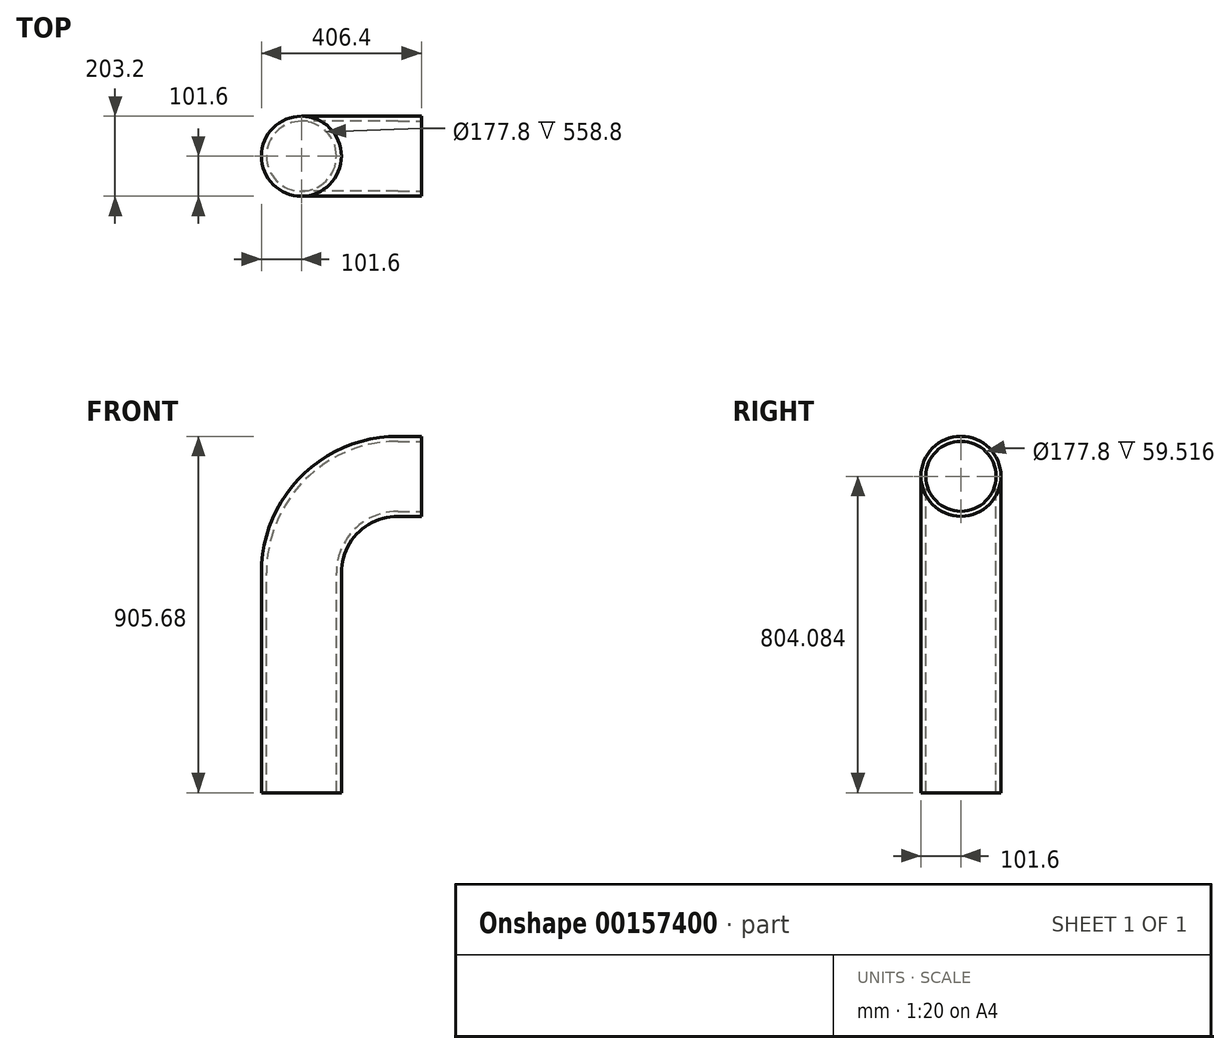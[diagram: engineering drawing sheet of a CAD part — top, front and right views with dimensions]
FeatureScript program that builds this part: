
annotation { "Feature Type Name" : "Feature", "Feature Type Description" : "" }
export const myFeature = defineFeature(function(context is Context, id is Id, definition is map)
    precondition{}
    {
        {
            var Q0;
            Q0=qCreatedBy(makeId("Front.planeOp"),FACE);
            var sketch = newSketch(context, id + "F0", { "sketchPlane" : qUnion([Q0])});
            skLineSegment(sketch, "E0.bottom", {"start": v(0, 0) * mm, "end": v(203.2, 0) * mm});
            skLineSegment(sketch, "E0.left", {"start": v(0, 0) * mm, "end": v(0, 558.8) * mm});
            skLineSegment(sketch, "E0.right", {"start": v(203.2, 0) * mm, "end": v(203.2, 558.8) * mm});
            skLineSegment(sketch, "E1.bottom", {"start": v(346.88, 905.68) * mm, "end": v(609.6, 905.68) * mm});
            skLineSegment(sketch, "E1.right", {"start": v(609.6, 905.68) * mm, "end": v(609.6, 702.48) * mm});
            skArc(sketch, "E2", {"start": v(346.88, 702.48) * mm, "mid": v(245.28, 660.4) * mm, "end": v(203.2, 558.8) * mm});
            skArc(sketch, "E3", {"start": v(346.88, 905.68) * mm, "mid": v(101.6, 804.08) * mm, "end": v(0, 558.8) * mm});
            skLineSegment(sketch, "E4.trimOffspring", {"start": v(346.88, 702.48) * mm, "end": v(609.6, 702.48) * mm});
            skSolve(sketch);
        }
        {
            var Q0;
            Q0 = qSketchRegion(id + "F0", true);
            extrude(context, id + "F1", {"entities" : qUnion([Q0]), "depth" : 203.2 * mm});
        }
        {
            var Q0;
            Q0=makeQuery(id+"F1.opExtrude","CAP_EDGE",EDGE,{"disambiguationData":[OSD([sQuery(id+"F0.wireOp",EDGE,"E0.left")])],"isStart":false});
            var Q1;
            Q1=makeQuery(id+"F1.opExtrude","CAP_EDGE",EDGE,{"disambiguationData":[OSD([sQuery(id+"F0.wireOp",EDGE,"E0.right")])],"isStart":false});
            var Q2;
            Q2=makeQuery(id+"F1.opExtrude","CAP_EDGE",EDGE,{"disambiguationData":[OSD([sQuery(id+"F0.wireOp",EDGE,"E0.left")])],"isStart":true});
            var Q3;
            Q3=makeQuery(id+"F1.opExtrude","CAP_EDGE",EDGE,{"disambiguationData":[OSD([sQuery(id+"F0.wireOp",EDGE,"E0.right")])],"isStart":true});
            fillet(context, id + "F2", {"entities" : qUnion([Q0, Q1, Q2, Q3]), "radius" : 101.6 * mm, "tangentPropagation" : true, "allowEdgeOverflow" : false});
        }
        {
            var Q0;
            Q0=makeQuery(id+"F1.opExtrude","SWEPT_FACE",FACE,{"disambiguationData":[OSD([sQuery(id+"F0.wireOp",EDGE,"E0.bottom")])]});
            var Q1;
            Q1=makeQuery(id+"F1.opExtrude","SWEPT_FACE",FACE,{"disambiguationData":[OSD([sQuery(id+"F0.wireOp",EDGE,"E1.right")])]});
            shell(context, id + "F3", {"entities" : qUnion([Q0, Q1]), "thickness" : 12.7 * mm});
        }
        {
            var Q0;
            Q0=makeQuery(id+"F1.opExtrude","SWEPT_FACE",FACE,{"disambiguationData":[OSD([sQuery(id+"F0.wireOp",EDGE,"E1.right")])]});
            extrude(context, id + "F4", {"entities" : qUnion([Q0]), "operationType" : NewBodyOperationType.REMOVE, "oppositeDirection" : true, "depth" : 203.2 * mm});
        }
    });
